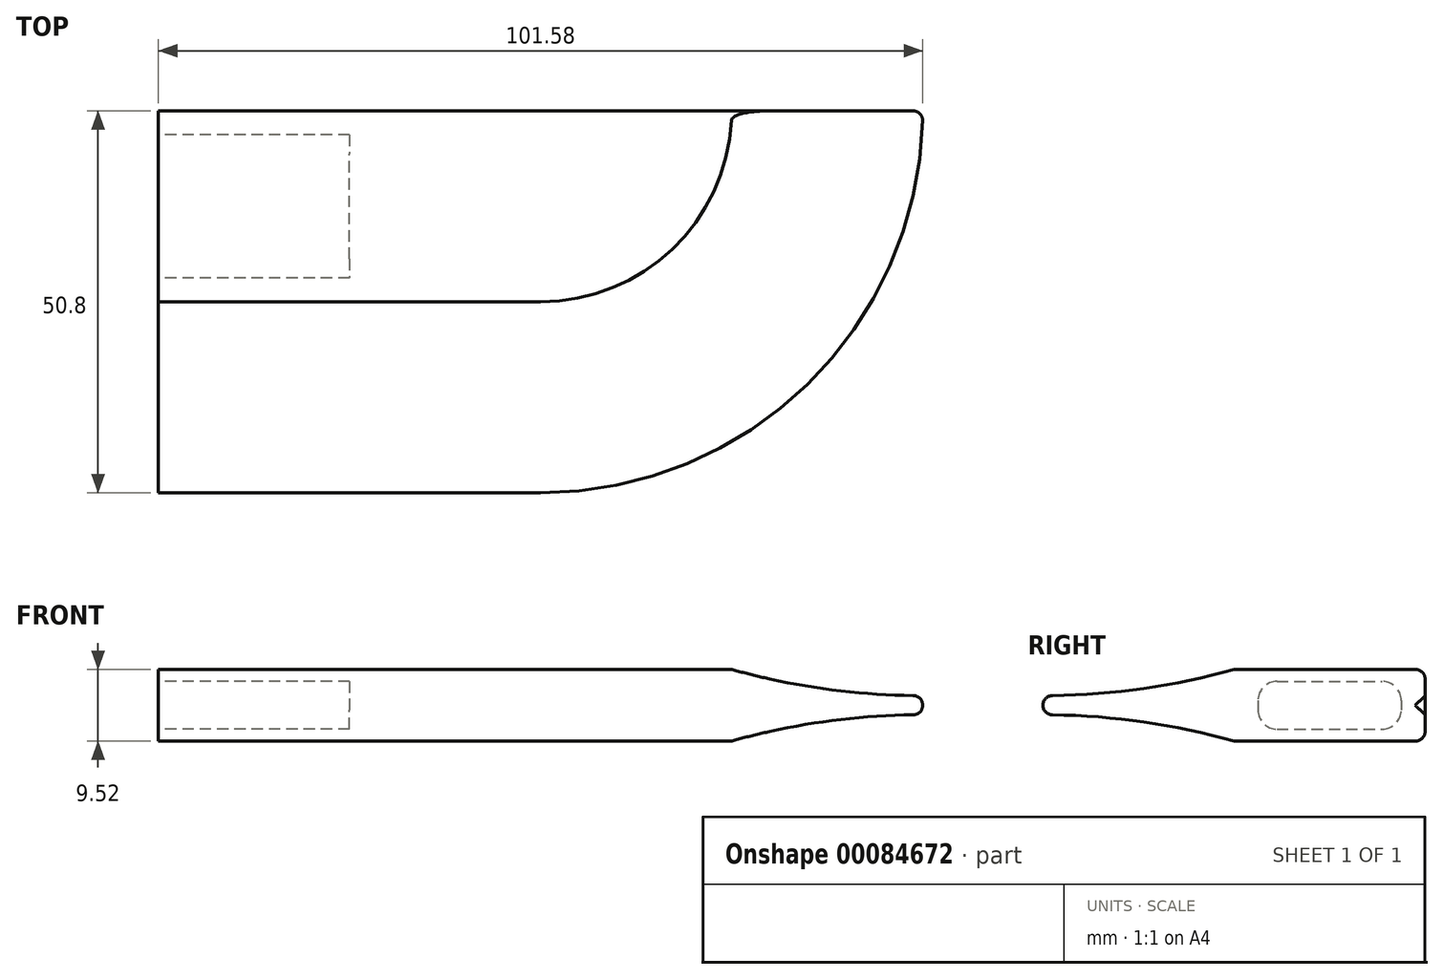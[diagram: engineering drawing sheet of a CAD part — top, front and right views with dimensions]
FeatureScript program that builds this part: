
annotation { "Feature Type Name" : "Feature", "Feature Type Description" : "" }
export const myFeature = defineFeature(function(context is Context, id is Id, definition is map)
    precondition{}
    {
        {
            var Q0;
            Q0=qCreatedBy(makeId("Top.planeOp"),FACE);
            var sketch = newSketch(context, id + "F0", { "sketchPlane" : qUnion([Q0])});
            skLineSegment(sketch, "E0", {"start": v(0, 0) * mm, "end": v(0, -50.8) * mm});
            skLineSegment(sketch, "E1", {"start": v(0, -50.8) * mm, "end": v(50.8, -50.8) * mm});
            skArc(sketch, "E2", {"start": v(50.8, -50.8) * mm, "mid": v(86.72, -35.92) * mm, "end": v(101.6, 0) * mm});
            skLineSegment(sketch, "E3", {"start": v(0, 0) * mm, "end": v(101.6, 0) * mm});
            skSolve(sketch);
        }
        {
            var Q0;
            Q0=makeQuery(id+"F0.imprint","IMPRINT",FACE,{"disambiguationData":[TD([[makeQuery(id+"F0.imprint","IMPRINT",EDGE,{"derivedFrom":sQuery(id+"F0.wireOp",EDGE,"E0")}),1.0]])]});
            extrude(context, id + "F1", {"entities" : qUnion([Q0]), "endBound" : BoundingType.SYMMETRIC, "depth" : 9.52 * mm});
        }
        {
            var Q0;
            Q0=qCreatedBy(makeId("Right.planeOp"),FACE);
            var sketch = newSketch(context, id + "F2", { "sketchPlane" : qUnion([Q0])});
            skLineSegment(sketch, "E4.bottom", {"start": v(-22.23, 3.18) * mm, "end": v(-3.17, 3.18) * mm});
            skLineSegment(sketch, "E4.top", {"start": v(-22.23, -3.17) * mm, "end": v(-3.17, -3.17) * mm});
            skLineSegment(sketch, "E4.left", {"start": v(-22.23, 3.18) * mm, "end": v(-22.23, -3.18) * mm});
            skLineSegment(sketch, "E4.right", {"start": v(-3.17, 3.18) * mm, "end": v(-3.17, -3.17) * mm});
            skLineSegment(sketch, "E5", {"start": v(-3.17, 3.18) * mm, "end": v(-22.23, -3.18) * mm, "construction": true});
            skLineSegment(sketch, "E6", {"start": v(-22.23, 3.18) * mm, "end": v(-3.17, -3.18) * mm, "construction": true});
            skPoint(sketch, "E7", {"position": v(-12.7, 0) * mm});
            skSolve(sketch);
        }
        {
            var Q0;
            Q0 = qSketchRegion(id + "F2", true);
            extrude(context, id + "F3", {"entities" : qUnion([Q0]), "operationType" : NewBodyOperationType.REMOVE, "depth" : 25.4 * mm});
        }
        {
            var Q0;
            Q0=makeQuery(id+"F3.boolean.opBoolean","COPY",EDGE,{"derivedFrom":makeQuery(id+"F3.opExtrude","SWEPT_EDGE",EDGE,{"disambiguationData":[OSD([sQuery(id+"F2.wireOp",EDGE,"E4.top"),sQuery(id+"F2.wireOp",EDGE,"E4.right")])]})});
            var Q1;
            Q1=makeQuery(id+"F3.boolean.opBoolean","COPY",EDGE,{"derivedFrom":makeQuery(id+"F3.opExtrude","SWEPT_EDGE",EDGE,{"disambiguationData":[OSD([sQuery(id+"F2.wireOp",EDGE,"E4.bottom"),sQuery(id+"F2.wireOp",EDGE,"E4.right")])]})});
            var Q2;
            Q2=makeQuery(id+"F3.boolean.opBoolean","COPY",EDGE,{"derivedFrom":makeQuery(id+"F3.opExtrude","SWEPT_EDGE",EDGE,{"disambiguationData":[OSD([sQuery(id+"F2.wireOp",EDGE,"E4.top"),sQuery(id+"F2.wireOp",EDGE,"E4.left")])]})});
            var Q3;
            Q3=makeQuery(id+"F3.boolean.opBoolean","COPY",EDGE,{"derivedFrom":makeQuery(id+"F3.opExtrude","SWEPT_EDGE",EDGE,{"disambiguationData":[OSD([sQuery(id+"F2.wireOp",EDGE,"E4.bottom"),sQuery(id+"F2.wireOp",EDGE,"E4.left")])]})});
            fillet(context, id + "F4", {"entities" : qUnion([Q0, Q1, Q2, Q3]), "radius" : 2.54 * mm, "tangentPropagation" : true, "allowEdgeOverflow" : false});
        }
        {
            var Q0;
            Q0=makeQuery(id+"F1.opExtrude","SWEPT_FACE",FACE,{"disambiguationData":[OSD([sQuery(id+"F0.wireOp",EDGE,"E0")])]});
            var sketch = newSketch(context, id + "F5", { "sketchPlane" : qUnion([Q0])});
            skArc(sketch, "E8", {"start": v(25.4, 4.76) * mm, "mid": v(37.98, 2.15) * mm, "end": v(50.8, 1.27) * mm});
            skLineSegment(sketch, "E9", {"start": v(50.8, 1.27) * mm, "end": v(60.98, 1.27) * mm, "construction": true});
            skLineSegment(sketch, "E10", {"start": v(25.4, 4.76) * mm, "end": v(50.8, 4.76) * mm});
            skLineSegment(sketch, "E11", {"start": v(50.8, 4.76) * mm, "end": v(50.8, 1.27) * mm});
            skSolve(sketch);
        }
        {
            var Q0;
            Q0 = qSketchRegion(id + "F5", true);
            var Q1;
            Q1=makeQuery(id+"F1.opExtrude","CAP_EDGE",EDGE,{"disambiguationData":[OSD([sQuery(id+"F0.wireOp",EDGE,"E1")])],"isStart":false});
            var Q2;
            Q2=makeQuery(id+"F1.opExtrude","CAP_EDGE",EDGE,{"disambiguationData":[OSD([sQuery(id+"F0.wireOp",EDGE,"E2")])],"isStart":false});
            sweep(context, id + "F6", {"profiles" : qUnion([Q0]), "path" : qUnion([Q1, Q2])});
        }
        {
            var Q0;
            Q0=makeQuery(id+"F6.opSweep","SWEPT_BODY",BODY,{"disambiguationData":[OSD([sQuery(id+"F0.wireOp",EDGE,"E2"),sQuery(id+"F5.wireOp",EDGE,"E8"),sQuery(id+"F5.wireOp",EDGE,"E10"),sQuery(id+"F5.wireOp",EDGE,"E11")])]});
            var Q1;
            Q1=qCreatedBy(makeId("Top.planeOp"),FACE);
            mirror(context, id + "F7", {"entities" : qUnion([Q0]), "mirrorPlane" : qUnion([Q1])});
        }
        {
            var Q0;
            Q0=makeQuery(id+"F6.opSweep","SWEPT_BODY",BODY,{"disambiguationData":[OSD([sQuery(id+"F0.wireOp",EDGE,"E2"),sQuery(id+"F5.wireOp",EDGE,"E8"),sQuery(id+"F5.wireOp",EDGE,"E10"),sQuery(id+"F5.wireOp",EDGE,"E11")])]});
            var Q1;
            Q1=makeQuery(id+"F7.opPattern","COPY",BODY,{"derivedFrom":makeQuery(id+"F6.opSweep","SWEPT_BODY",BODY,{"disambiguationData":[OSD([sQuery(id+"F0.wireOp",EDGE,"E2"),sQuery(id+"F5.wireOp",EDGE,"E8"),sQuery(id+"F5.wireOp",EDGE,"E10"),sQuery(id+"F5.wireOp",EDGE,"E11")])]}),"instanceName":"1"});
            var Q2;
            Q2=makeQuery(id+"F1.opExtrude","SWEPT_BODY",BODY,{"disambiguationData":[OSD([sQuery(id+"F0.wireOp",EDGE,"E0"),sQuery(id+"F0.wireOp",EDGE,"E1"),sQuery(id+"F0.wireOp",EDGE,"E2"),sQuery(id+"F0.wireOp",EDGE,"E3")])]});
            booleanBodies(context, id + "F8", {"operationType" : BooleanOperationType.SUBTRACTION, "tools" : qUnion([Q0, Q1]), "targets" : qUnion([Q2])});
        }
        {
            var Q0;
            Q0=makeQuery(id+"F8.opBoolean","COPY",EDGE,{"derivedFrom":makeQuery(id+"F6.opSweep","SWEPT_EDGE",EDGE,{"disambiguationData":[OSD([sQuery(id+"F0.wireOp",EDGE,"E0"),sQuery(id+"F0.wireOp",EDGE,"E1"),sQuery(id+"F5.wireOp",EDGE,"E8"),sQuery(id+"F5.wireOp",EDGE,"E11")])]})});
            var Q1;
            Q1=makeQuery(id+"F8.opBoolean","COPY",EDGE,{"derivedFrom":makeQuery(id+"F7.opPattern","COPY",EDGE,{"derivedFrom":makeQuery(id+"F6.opSweep","SWEPT_EDGE",EDGE,{"disambiguationData":[OSD([sQuery(id+"F0.wireOp",EDGE,"E0"),sQuery(id+"F0.wireOp",EDGE,"E1"),sQuery(id+"F5.wireOp",EDGE,"E8"),sQuery(id+"F5.wireOp",EDGE,"E11")])]}),"instanceName":"1"})});
            var Q2;
            Q2=makeQuery(id+"F1.opExtrude","SWEPT_FACE",FACE,{"disambiguationData":[OSD([sQuery(id+"F0.wireOp",EDGE,"E2")])]});
            fillet(context, id + "F9", {"entities" : qUnion([Q0, Q1, Q2]), "radius" : 1.27 * mm, "tangentPropagation" : true, "allowEdgeOverflow" : false});
        }
        {
            var Q0;
            Q0=makeQuery(id+"F1.opExtrude","CAP_EDGE",EDGE,{"disambiguationData":[OSD([sQuery(id+"F0.wireOp",EDGE,"E3")])],"isStart":false});
            var Q1;
            Q1=makeQuery(id+"F1.opExtrude","CAP_EDGE",EDGE,{"disambiguationData":[OSD([sQuery(id+"F0.wireOp",EDGE,"E3")])],"isStart":true});
            fillet(context, id + "F10", {"entities" : qUnion([Q0, Q1]), "radius" : 1.27 * mm, "tangentPropagation" : true, "allowEdgeOverflow" : false});
        }
    });
